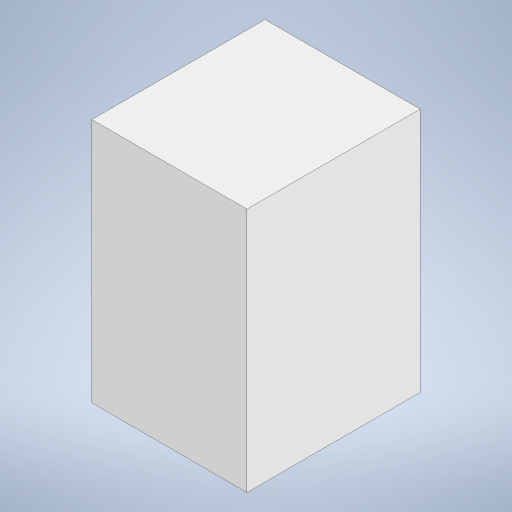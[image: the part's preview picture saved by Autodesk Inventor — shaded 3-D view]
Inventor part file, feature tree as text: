
AUTODESK INVENTOR PART (.ipt)
format: ipt  version: 2024 (Build 280153000, 153)  size: 174,080 bytes
history: native  units: in
note: dims shown in document units (in); Inventor stores cm internally (conversion verified against a paired STEP export)
features: extrude x1, sketch x1
ambient origin geometry x8: Origin, YZ Plane, XZ Plane, XY Plane, X Axis, Y Axis, Z Axis, Center Point
bodies: Solid1 (feature_tree)
feature tree (2):
  extrude  "Extrusion1"  Depth=24.0in
  sketch  "Sketch1"  dims[d1=34.0in d2=24.0in d3=21.5in d4=0.0in]
